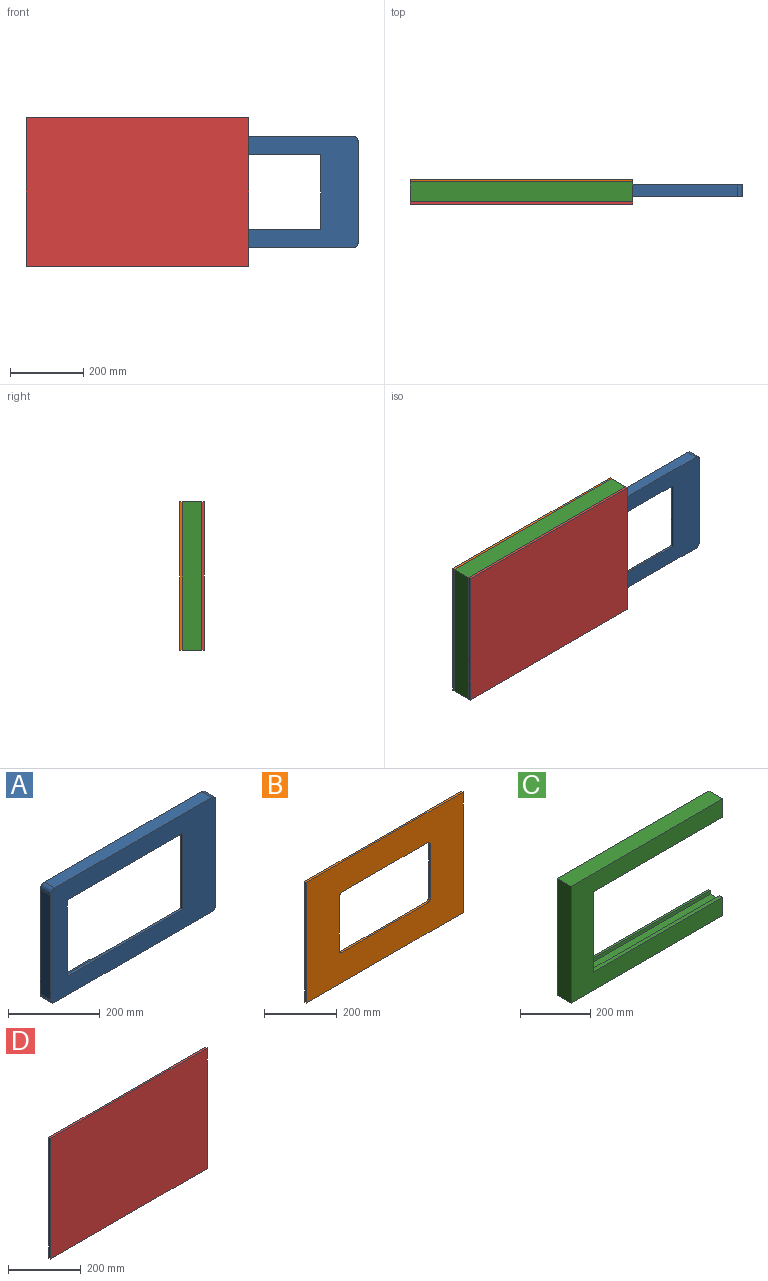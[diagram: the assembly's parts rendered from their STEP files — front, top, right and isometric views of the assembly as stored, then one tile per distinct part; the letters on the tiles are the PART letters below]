
ASSEMBLY  parts=4 mates=9
PART A: 32 faces, bbox 508x31.8x304.8 mm
  f0: plane 482.6x254mm, normal (0,1,0), area 34548mm2, adj f5,f6,f7,f8,f9,f10,f11,f12
  f1: plane 6.23x4.12mm, normal (-1,0,0), area 8.3mm2, adj f12,f18,f28
  f2: plane 6.23x4.12mm, normal (1,0,0), area 8.3mm2, adj f12,f18,f28
  f3: plane 279.4x31.75mm, normal (-1,0,0), area 8870.9mm2, adj f18,f23,f26,f27
  f4: plane 482.6x31.75mm, normal (0,0,1), area 15322.6mm2, adj f18,f23,f25,f26
  f5: plane 279.4x31.75mm, normal (1,0,0), area 8333.3mm2, adj f0,f6,f16,f18,f23,f24,f25
  f6: plane 38.1x25.4mm, normal (0,0,-1), area 967.7mm2, adj f0,f5,f7,f18
  f7: plane 112.6x25.4mm, normal (1,0,0), area 2860mm2, adj f0,f6,f8,f18
  f8: plane 38.1x25.4mm, normal (0,0,-1), area 967.7mm2, adj f0,f7,f9,f18
  f9: plane 112.6x25.4mm, normal (-1,0,0), area 2860mm2, adj f0,f8,f10,f18
  f10: plane 406.4x25.4mm, normal (0,0,-1), area 9871.4mm2, adj f0,f9,f11,f18,f29,f30,f31
  f11: plane 254x25.4mm, normal (1,0,0), area 6451.6mm2, adj f0,f10,f12,f18
  f12: plane 406.4x25.4mm, normal (0,0,1), area 9871.5mm2, adj f0,f1,f2,f11,f13,f18,f28
  f13: plane 109.66x25.4mm, normal (-1,0,0), area 2785.3mm2, adj f0,f12,f14,f18
  f14: plane 50.8x25.4mm, normal (0,0,1), area 1290.3mm2, adj f0,f13,f15,f18
  f15: plane 123.17x25.4mm, normal (-1,0,0), area 3128.6mm2, adj f0,f14,f16,f18
  f16: plane 25.4x25.4mm, normal (0,0,1), area 645.2mm2, adj f0,f5,f15,f18
  f17: plane 482.6x31.75mm, normal (0,0,-1), area 15322.6mm2, adj f18,f23,f24,f27
  f18: plane 508x304.8mm, normal (0,1,0), area 48426.3mm2, adj f1,f2,f3,f4,f5,f6,f7,f8
  f19: plane 203.2x6.35mm, normal (-1,0,0), area 1290.3mm2, adj f0,f20,f22,f23
  f20: plane 355.6x6.35mm, normal (0,0,1), area 2258.1mm2, adj f0,f19,f21,f23
  f21: plane 203.2x6.35mm, normal (1,0,0), area 1290.3mm2, adj f0,f20,f22,f23
  f22: plane 355.6x6.35mm, normal (0,0,-1), area 2258.1mm2, adj f0,f19,f21,f23
  f23: plane 508x304.8mm, normal (0,-1,0), area 82442mm2, adj f3,f4,f5,f17,f19,f20,f21,f22
  f24: cylinder r=12.7mm len=31.75mm, axis (0,1,0), area 633.4mm2, adj f5,f17,f18,f23
  f25: cylinder r=12.7mm len=31.75mm, axis (0,1,0), area 633.4mm2, adj f4,f5,f18,f23
  f26: cylinder r=12.7mm len=31.75mm, axis (0,1,0), area 633.4mm2, adj f3,f4,f18,f23
  f27: cylinder r=12.7mm len=31.75mm, axis (0,1,0), area 633.4mm2, adj f3,f17,f18,f23
  f28: extruded ~76.2x5.92mm, area 623mm2, adj f1,f2,f12,f18
  f29: plane 7.44x4.15mm, normal (1,0,0), area 8mm2, adj f10,f18,f31
  f30: plane 7.44x4.15mm, normal (-1,0,0), area 8mm2, adj f10,f18,f31
  f31: extruded ~63.5x7.11mm, area 600.2mm2, adj f10,f18,f29,f30
PART B: 14 faces, bbox 609.6x6.4x406.4 mm
  f0: plane 406.4x6.35mm, normal (1,0,0), area 2580.6mm2, adj f1,f7,f8,f9
  f1: plane 609.6x6.35mm, normal (0,0,1), area 3871mm2, adj f0,f2,f8,f9
  f2: plane 406.4x6.35mm, normal (-1,0,0), area 2580.6mm2, adj f1,f7,f8,f9
  f3: plane 330.2x6.35mm, normal (0,0,-1), area 2096.8mm2, adj f8,f9,f10,f13
  f4: plane 177.8x6.35mm, normal (-1,0,0), area 1129mm2, adj f8,f9,f10,f11
  f5: plane 330.2x6.35mm, normal (0,0,1), area 2096.8mm2, adj f8,f9,f11,f12
  f6: plane 177.8x6.35mm, normal (1,0,0), area 1129mm2, adj f8,f9,f12,f13
  f7: plane 609.6x6.35mm, normal (0,0,-1), area 3871mm2, adj f0,f2,f8,f9
  f8: plane 609.6x406.4mm, normal (0,-1,0), area 175622mm2, adj f0,f1,f2,f3,f4,f5,f6,f7
  f9: plane 609.6x406.4mm, normal (0,1,0), area 175622mm2, adj f0,f1,f2,f3,f4,f5,f6,f7
  f10: cylinder r=12.7mm len=12.7mm, axis (0,-1,0), area 126.7mm2, adj f3,f4,f8,f9
  f11: cylinder r=12.7mm len=12.7mm, axis (0,1,0), area 126.7mm2, adj f4,f5,f8,f9
  f12: cylinder r=12.7mm len=12.7mm, axis (0,-1,0), area 126.7mm2, adj f5,f6,f8,f9
  f13: cylinder r=12.7mm len=12.7mm, axis (0,1,0), area 126.7mm2, adj f3,f6,f8,f9
PART C: 18 faces, bbox 609.6x54.6x406.4 mm
  f0: plane 609.6x54.61mm, normal (0,0,1), area 33290.3mm2, adj f6,f11,f12,f16
  f1: plane 609.6x54.61mm, normal (0,0,-1), area 33290.3mm2, adj f6,f11,f12,f17
  f2: plane 533.4x35.56mm, normal (0,0,-1), area 18967.7mm2, adj f7,f8,f13,f16
  f3: plane 533.4x35.56mm, normal (0,0,1), area 18967.7mm2, adj f7,f8,f13,f17
  f4: plane 520.7x6.35mm, normal (0,0,-1), area 3306.4mm2, adj f6,f7,f14,f16
  f5: plane 520.7x6.35mm, normal (0,0,1), area 3306.4mm2, adj f6,f7,f14,f17
  f6: plane 609.6x406.4mm, normal (0,1,0), area 102257.9mm2, adj f0,f1,f4,f5,f12,f14,f16,f17
  f7: plane 533.4x304.8mm, normal (0,-1,0), area 17096.7mm2, adj f2,f3,f4,f5,f13,f14,f16,f17
  f8: plane 533.4x304.8mm, normal (0,1,0), area 17096.7mm2, adj f2,f3,f9,f10,f13,f15,f16,f17
  f9: plane 520.7x12.7mm, normal (0,0,-1), area 6612.9mm2, adj f8,f11,f15,f16
  f10: plane 520.7x12.7mm, normal (0,0,1), area 6612.9mm2, adj f8,f11,f15,f17
  f11: plane 609.6x406.4mm, normal (0,-1,0), area 102257.9mm2, adj f0,f1,f9,f10,f12,f15,f16,f17
  f12: plane 406.4x54.61mm, normal (-1,0,0), area 22193.5mm2, adj f0,f1,f6,f11
  f13: plane 304.8x35.56mm, normal (1,0,0), area 10838.7mm2, adj f2,f3,f7,f8
  f14: plane 279.4x6.35mm, normal (1,0,0), area 1774.2mm2, adj f4,f5,f6,f7
  f15: plane 279.4x12.7mm, normal (1,0,0), area 3548.4mm2, adj f8,f9,f10,f11
  f16: plane 63.5x54.61mm, normal (1,0,0), area 3016.1mm2, adj f0,f2,f4,f6,f7,f8,f9,f11
  f17: plane 63.5x54.61mm, normal (1,0,0), area 3016.1mm2, adj f1,f3,f5,f6,f7,f8,f10,f11
PART D: 6 faces, bbox 609.6x6.4x406.4 mm
  f0: plane 406.4x6.35mm, normal (-1,0,0), area 2580.6mm2, adj f1,f3,f4,f5
  f1: plane 609.6x6.35mm, normal (0,0,-1), area 3871mm2, adj f0,f2,f4,f5
  f2: plane 406.4x6.35mm, normal (1,0,0), area 2580.6mm2, adj f1,f3,f4,f5
  f3: plane 609.6x6.35mm, normal (0,0,1), area 3871mm2, adj f0,f2,f4,f5
  f4: plane 609.6x406.4mm, normal (0,-1,0), area 247741.4mm2, adj f0,f1,f2,f3
  f5: plane 609.6x406.4mm, normal (0,1,0), area 247741.4mm2, adj f0,f1,f2,f3
PLACE A t=(292.88,-10.08,-8.56)mm
PLACE B t=(-31.07,17.22,-8.56)mm
PLACE C t=(-5.67,4.52,-8.56)mm fixed
PLACE D t=(-1141.83,-43.74,-8.56)mm
MATE planar C.f6 <-> B.f8  axis (0,1,0) through (-246.97,10.87,131.14)mm
MATE planar A.f4 <-> C.f2  axis (0,0,1) through (318.28,-13.26,143.84)mm
MATE parallel D.f2 <-> C.f16  axis (1,0,0) through (273.73,-46.91,-8.56)mm
MATE planar B.f2 <-> C.f12  axis (-1,0,0) through (-335.87,14.05,-8.56)mm
MATE slider C.f13 <-> A.f3  axis (1,0,0) through (-259.67,-13.26,-8.56)mm
MATE parallel A.f18 <-> C.f7  axis (0,1,0) through (356.05,2.62,-12.02)mm
MATE planar C.f11 <-> D.f5  axis (0,-1,0) through (-94.31,-43.74,-8.56)mm
MATE planar B.f1 <-> C.f0  axis (0,0,1) through (-31.07,14.05,194.64)mm
MATE parallel D.f3 <-> C.f0  axis (0,0,1) through (-31.07,-46.91,194.64)mm
